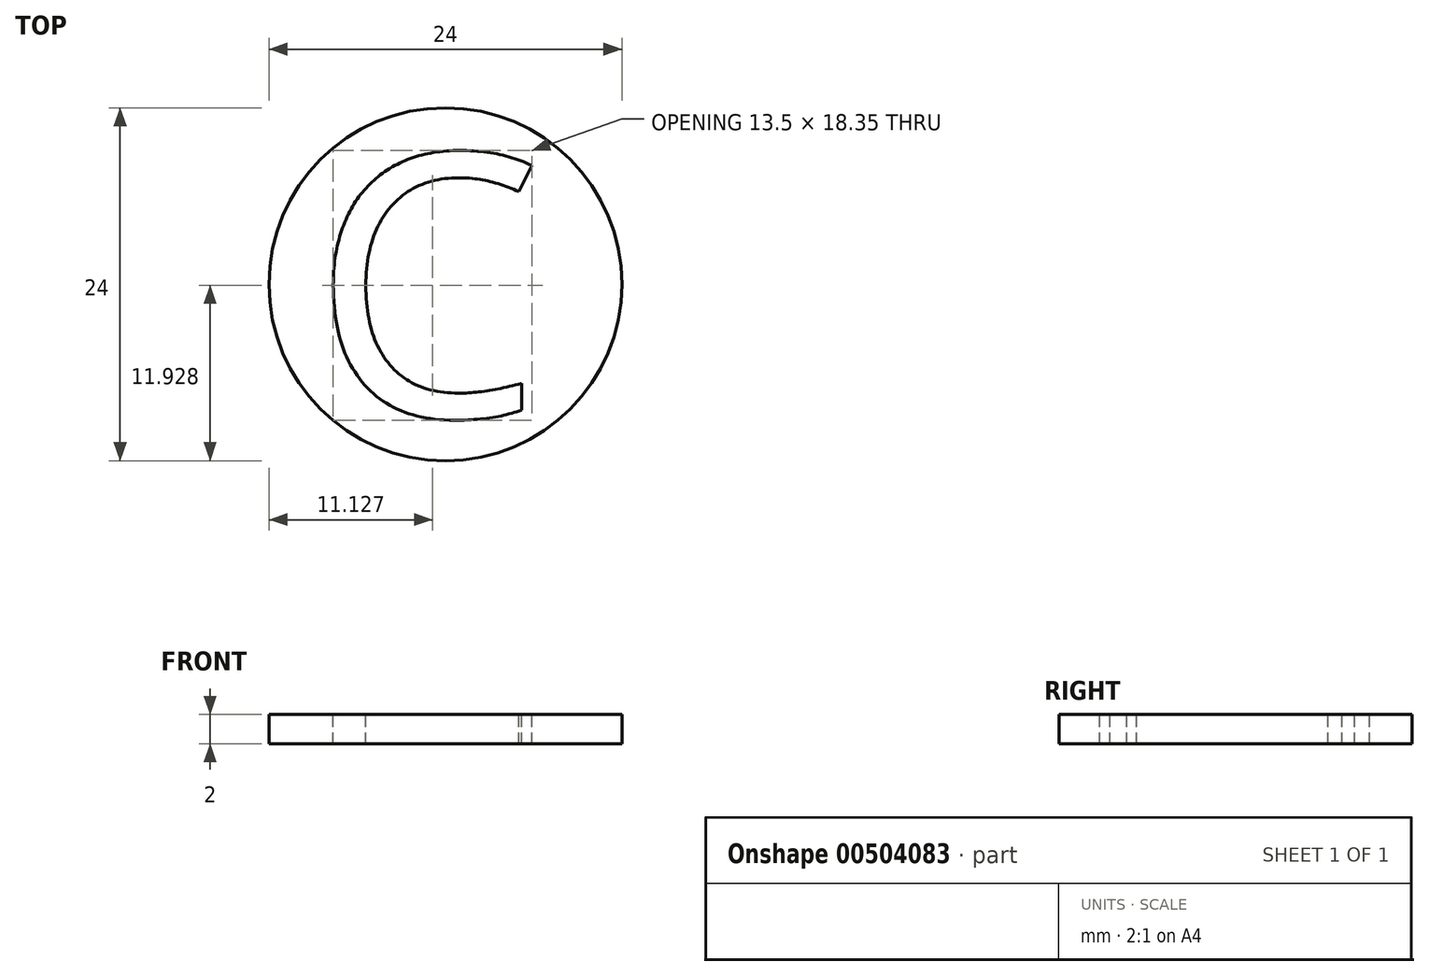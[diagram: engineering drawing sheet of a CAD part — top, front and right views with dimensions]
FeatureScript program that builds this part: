
annotation { "Feature Type Name" : "Feature", "Feature Type Description" : "" }
export const myFeature = defineFeature(function(context is Context, id is Id, definition is map)
    precondition{}
    {
        {
            var Q0;
            Q0=qCreatedBy(makeId("Top.planeOp"),FACE);
            var sketch = newSketch(context, id + "F0", { "sketchPlane" : qUnion([Q0])});
            skCircle(sketch, "E0", {"center": v(0, 0) * mm, "radius": 12 * mm});
            skSolve(sketch);
        }
        {
            var Q0;
            Q0=qSketchRegion(id+"F0",true);
            extrude(context, id + "F1", {"entities" : qUnion([Q0]), "depth" : 2 * mm});
        }
        {
            var Q0;
            Q0=makeQuery(id+"F1.opExtrude","CAP_FACE",FACE,{"disambiguationData":[OSD([sQuery(id+"F0.wireOp",EDGE,"E0")])],"isStart":false});
            var sketch = newSketch(context, id + "F2", { "sketchPlane" : qUnion([Q0])});
            skText(sketch, "E1", { "text": "C", "fontName": "OpenSans-Regular.ttf"});
            skPoint(sketch, "E2", {"position": v(7.5, 0) * mm});
            const initialGuessF2  = {"E1": [-0.00915, -0.009, 1, 0, 0.018]};
            skSetInitialGuess(sketch, initialGuessF2);
            skSolve(sketch);
        }
        {
            var Q0;
            Q0 = qSketchRegion(id + "F2", true);
            extrude(context, id + "F3", {"entities" : qUnion([Q0]), "operationType" : NewBodyOperationType.REMOVE, "oppositeDirection" : true, "depth" : 25 * mm, "offsetDistance" : 25 * mm});
        }
    });
